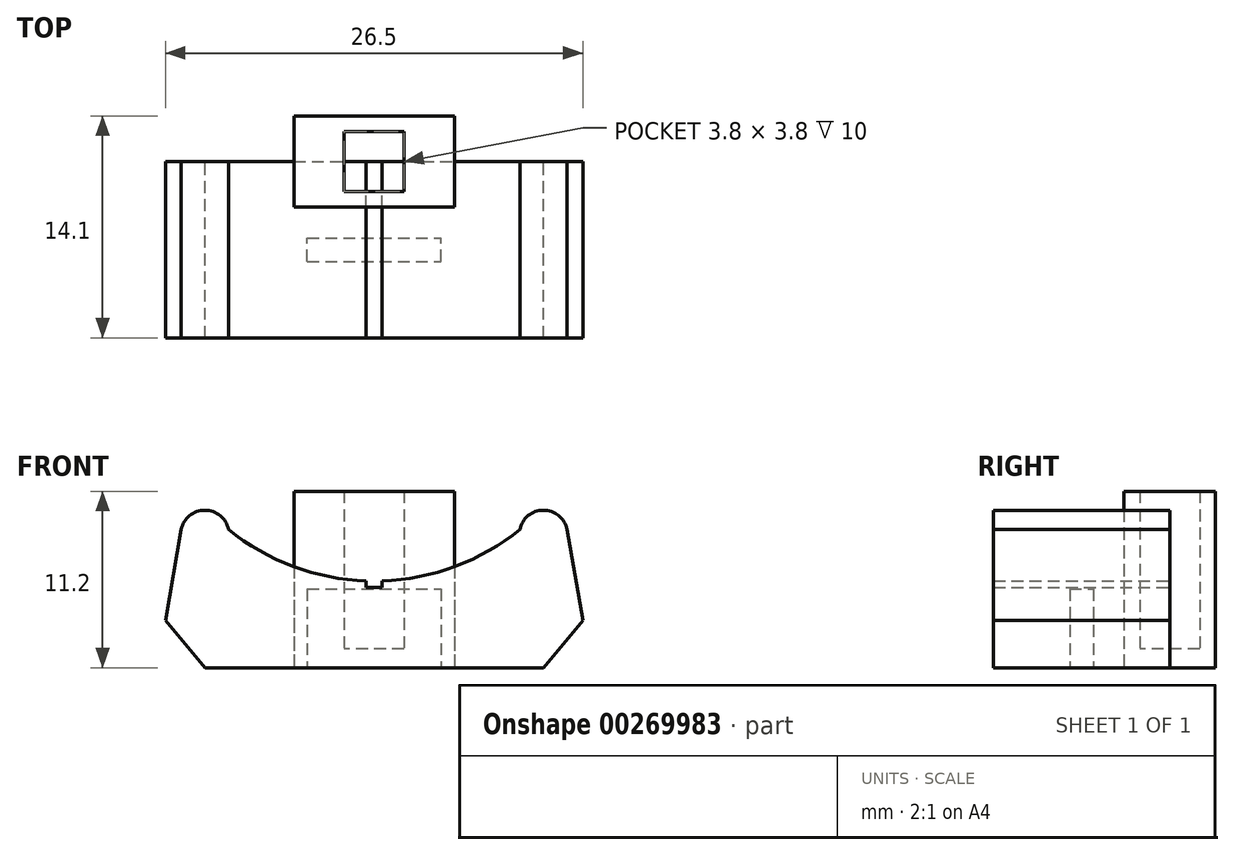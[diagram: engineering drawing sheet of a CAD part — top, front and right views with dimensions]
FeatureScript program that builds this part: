
annotation { "Feature Type Name" : "Feature", "Feature Type Description" : "" }
export const myFeature = defineFeature(function(context is Context, id is Id, definition is map)
    precondition{}
    {
        {
            var Q0;
            Q0=qCreatedBy(makeId("Top.planeOp"),FACE);
            var sketch = newSketch(context, id + "F0", { "sketchPlane" : qUnion([Q0])});
            skLineSegment(sketch, "E0.bottom", {"start": v(5.1, 2.9) * mm, "end": v(-5.1, 2.9) * mm});
            skLineSegment(sketch, "E0.top", {"start": v(5.1, -2.9) * mm, "end": v(-5.1, -2.9) * mm});
            skLineSegment(sketch, "E0.left", {"start": v(5.1, 2.9) * mm, "end": v(5.1, -2.9) * mm});
            skLineSegment(sketch, "E0.right", {"start": v(-5.1, 2.9) * mm, "end": v(-5.1, -2.9) * mm});
            skPoint(sketch, "E0.middle", {"position": v(0, 0) * mm});
            skLineSegment(sketch, "E1.bottom", {"start": v(1.9, 1.9) * mm, "end": v(-1.9, 1.9) * mm});
            skLineSegment(sketch, "E1.top", {"start": v(1.9, -1.9) * mm, "end": v(-1.9, -1.9) * mm});
            skLineSegment(sketch, "E1.left", {"start": v(1.9, 1.9) * mm, "end": v(1.9, -1.9) * mm});
            skLineSegment(sketch, "E1.right", {"start": v(-1.9, 1.9) * mm, "end": v(-1.9, -1.9) * mm});
            skSolve(sketch);
        }
        {
            var Q0;
            Q0=makeQuery(id+"F0.imprint","IMPRINT",FACE,{"disambiguationData":[TD([[makeQuery(id+"F0.imprint","IMPRINT",EDGE,{"derivedFrom":sQuery(id+"F0.wireOp",EDGE,"E1.bottom")}),1.0]])]});
            extrude(context, id + "F1", {"entities" : qUnion([Q0]), "depth" : 1.2 * mm, "offsetDistance" : 25 * mm});
        }
        {
            var Q0;
            Q0=makeQuery(id+"F0.imprint","IMPRINT",FACE,{"disambiguationData":[TD([[makeQuery(id+"F0.imprint","IMPRINT",EDGE,{"derivedFrom":sQuery(id+"F0.wireOp",EDGE,"E0.bottom")}),1.0]])]});
            extrude(context, id + "F2", {"entities" : qUnion([Q0]), "operationType" : NewBodyOperationType.ADD, "depth" : 11.2 * mm, "offsetDistance" : 25 * mm});
        }
        {
            var Q0;
            Q0=qCreatedBy(makeId("Front.planeOp"),FACE);
            var sketch = newSketch(context, id + "F3", { "sketchPlane" : qUnion([Q0])});
            skLineSegment(sketch, "E2", {"start": v(-10.75, 0) * mm, "end": v(10.75, 0) * mm});
            skPoint(sketch, "E3", {"position": v(0, 0) * mm});
            skLineSegment(sketch, "E4", {"start": v(-10.75, 10) * mm, "end": v(10.75, 10) * mm, "construction": true});
            skPoint(sketch, "E5", {"position": v(0, 5.5) * mm});
            skPoint(sketch, "E6", {"position": v(-13.25, 3) * mm});
            skPoint(sketch, "E7", {"position": v(13.25, 3) * mm});
            skLineSegment(sketch, "E8", {"start": v(-13.25, 3) * mm, "end": v(13.25, 3) * mm, "construction": true});
            skPoint(sketch, "E9", {"position": v(0, 3) * mm});
            skLineSegment(sketch, "E10", {"start": v(-13.25, 3) * mm, "end": v(-10.75, 0) * mm});
            skLineSegment(sketch, "E11", {"start": v(10.75, 0) * mm, "end": v(13.25, 3) * mm});
            skArc(sketch, "E12", {"start": v(-9.25, 8.77) * mm, "mid": v(-10.75, 10) * mm, "end": v(-12.25, 8.77) * mm});
            skPoint(sketch, "E13", {"position": v(-10.75, 10) * mm});
            skLineSegment(sketch, "E14", {"start": v(-12.25, 8.77) * mm, "end": v(-13.25, 3) * mm});
            skArc(sketch, "E15.MirrorCS", {"start": v(9.25, 8.77) * mm, "mid": v(10.75, 10) * mm, "end": v(12.25, 8.77) * mm});
            skLineSegment(sketch, "E16.MirrorCS", {"start": v(12.25, 8.77) * mm, "end": v(13.25, 3) * mm});
            skArc(sketch, "E17", {"start": v(-9.25, 8.77) * mm, "mid": v(-5.14, 6.43) * mm, "end": v(-0.5, 5.5) * mm});
            skLineSegment(sketch, "E18.bottom", {"start": v(0.5, 5.1) * mm, "end": v(-0.5, 5.1) * mm});
            skLineSegment(sketch, "E18.left", {"start": v(0.5, 5.1) * mm, "end": v(0.5, 5.5) * mm});
            skLineSegment(sketch, "E18.right", {"start": v(-0.5, 5.1) * mm, "end": v(-0.5, 5.5) * mm});
            skArc(sketch, "E19.trimOffspring", {"start": v(0.5, 5.5) * mm, "mid": v(5.14, 6.43) * mm, "end": v(9.25, 8.77) * mm});
            skSolve(sketch);
        }
        {
            var Q0;
            Q0=makeQuery(id+"F3.imprint","IMPRINT",FACE,{"disambiguationData":[TD([[makeQuery(id+"F3.imprint","IMPRINT",EDGE,{"derivedFrom":sQuery(id+"F3.wireOp",EDGE,"E2")}),1.0]])]});
            extrude(context, id + "F4", {"entities" : qUnion([Q0]), "depth" : 11.2 * mm, "offsetDistance" : 25 * mm});
        }
        {
            var Q0;
            Q0=makeQuery(id+"F4.opExtrude","SWEPT_FACE",FACE,{"disambiguationData":[OSD([sQuery(id+"F3.wireOp",EDGE,"E2")])]});
            var sketch = newSketch(context, id + "F5", { "sketchPlane" : qUnion([Q0])});
            skLineSegment(sketch, "E20.bottom", {"start": v(-4.25, 6.35) * mm, "end": v(4.25, 6.35) * mm});
            skLineSegment(sketch, "E20.top", {"start": v(-4.25, 4.85) * mm, "end": v(4.25, 4.85) * mm});
            skLineSegment(sketch, "E20.left", {"start": v(-4.25, 6.35) * mm, "end": v(-4.25, 4.85) * mm});
            skLineSegment(sketch, "E20.right", {"start": v(4.25, 6.35) * mm, "end": v(4.25, 4.85) * mm});
            skPoint(sketch, "E20.middle", {"position": v(0, 5.6) * mm});
            skPoint(sketch, "E20.middle.positionSnap0", {"position": v(-10.75, 5.6) * mm});
            skPoint(sketch, "E20.centerSnap0", {"position": v(-10.75, 5.6) * mm});
            skSolve(sketch);
        }
        {
            var Q0;
            Q0=makeQuery(id+"F5.imprint","IMPRINT",FACE,{"disambiguationData":[TD([[makeQuery(id+"F5.imprint","IMPRINT",EDGE,{"derivedFrom":sQuery(id+"F5.wireOp",EDGE,"E20.bottom")}),-1.0]])]});
            extrude(context, id + "F6", {"entities" : qUnion([Q0]), "operationType" : NewBodyOperationType.REMOVE, "oppositeDirection" : true, "depth" : 5 * mm, "offsetDistance" : 25 * mm});
        }
    });
